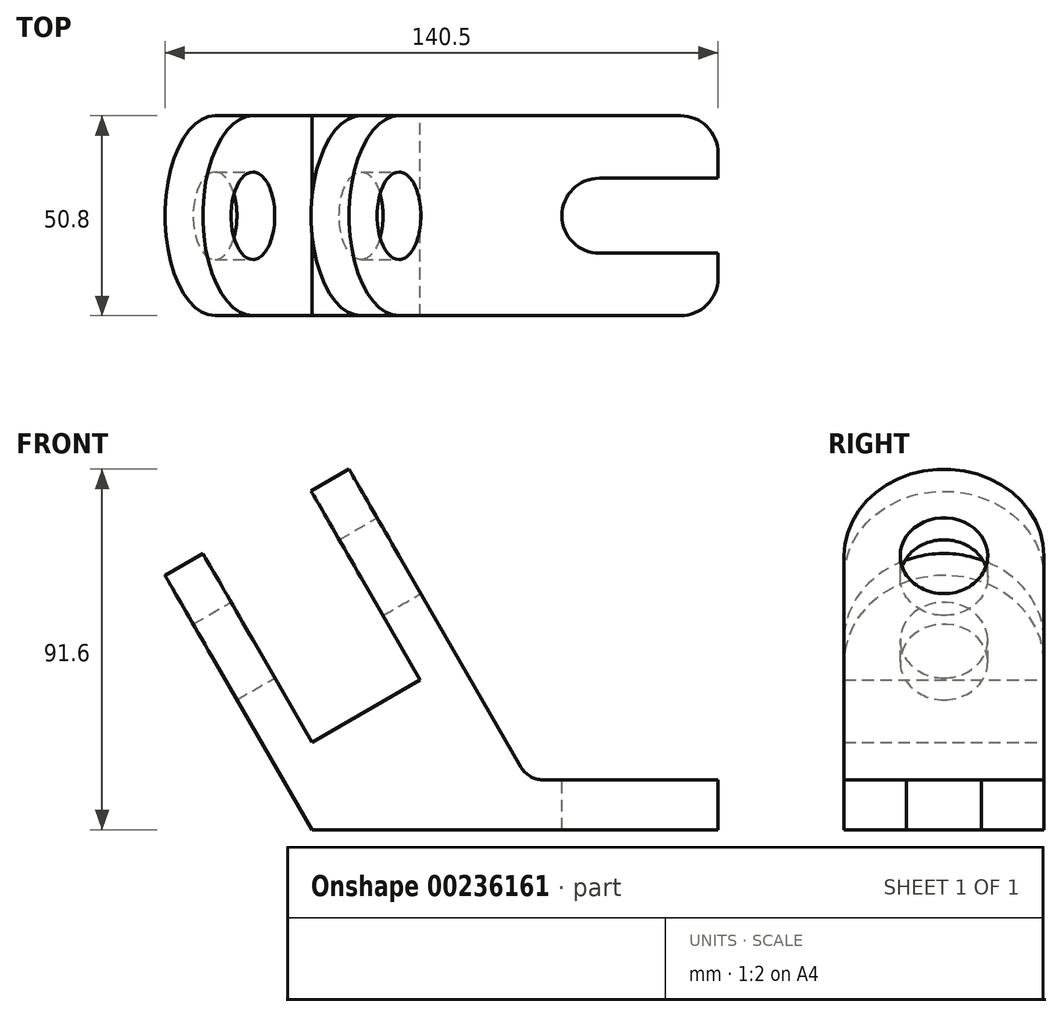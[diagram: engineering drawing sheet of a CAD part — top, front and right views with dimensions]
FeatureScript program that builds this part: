
annotation { "Feature Type Name" : "Feature", "Feature Type Description" : "" }
export const myFeature = defineFeature(function(context is Context, id is Id, definition is map)
    precondition{}
    {
        {
            var Q0;
            Q0=qCreatedBy(makeId("Front.planeOp"),FACE);
            var sketch = newSketch(context, id + "F0", { "sketchPlane" : qUnion([Q0])});
            skLineSegment(sketch, "E0", {"start": v(0, 0) * mm, "end": v(103.19, 0) * mm});
            skLineSegment(sketch, "E1", {"start": v(103.19, 0) * mm, "end": v(103.19, 12.7) * mm});
            skLineSegment(sketch, "E2", {"start": v(103.19, 12.7) * mm, "end": v(58.66, 12.7) * mm});
            skLineSegment(sketch, "E3", {"start": v(53.16, 15.88) * mm, "end": v(9.44, 91.6) * mm});
            skLineSegment(sketch, "E4", {"start": v(9.44, 91.6) * mm, "end": v(-0.19, 86.05) * mm});
            skLineSegment(sketch, "E5", {"start": v(-37.3, 64.62) * mm, "end": v(0, 0) * mm});
            skLineSegment(sketch, "E6", {"start": v(-27.68, 70.17) * mm, "end": v(0, 22.22) * mm});
            skLineSegment(sketch, "E7", {"start": v(0, 22.23) * mm, "end": v(27.5, 38.1) * mm});
            skLineSegment(sketch, "E8", {"start": v(27.5, 38.1) * mm, "end": v(-0.19, 86.05) * mm});
            skLineSegment(sketch, "E9.trimOffspring", {"start": v(-27.68, 70.17) * mm, "end": v(-37.3, 64.62) * mm});
            skPoint(sketch, "E10.visualSharp", {"position": v(55, 12.7) * mm});
            skArc(sketch, "E10.filletArc", {"start": v(53.16, 15.88) * mm, "mid": v(55.48, 13.55) * mm, "end": v(58.66, 12.7) * mm});
            skSolve(sketch);
        }
        {
            var Q0;
            Q0=makeQuery(id+"F0.imprint","IMPRINT",FACE,{"disambiguationData":[TD([[makeQuery(id+"F0.imprint","IMPRINT",EDGE,{"derivedFrom":sQuery(id+"F0.wireOp",EDGE,"E0")}),1.0]])]});
            extrude(context, id + "F1", {"entities" : qUnion([Q0]), "endBound" : BoundingType.SYMMETRIC, "depth" : 50.8 * mm});
        }
        {
            var Q0;
            Q0=makeQuery(id+"F1.opExtrude","SWEPT_FACE",FACE,{"disambiguationData":[OSD([sQuery(id+"F0.wireOp",EDGE,"E2")])]});
            var sketch = newSketch(context, id + "F2", { "sketchPlane" : qUnion([Q0])});
            skArc(sketch, "E11", {"start": v(73.03, 9.53) * mm, "mid": v(63.5, 0) * mm, "end": v(73.03, -9.53) * mm});
            skPoint(sketch, "E11.centerSnap0", {"position": v(103.19, 0) * mm});
            skLineSegment(sketch, "E12", {"start": v(73.03, 9.53) * mm, "end": v(103.19, 9.53) * mm});
            skLineSegment(sketch, "E13", {"start": v(73.03, -9.53) * mm, "end": v(103.19, -9.52) * mm});
            skLineSegment(sketch, "E14.0", {"start": v(103.19, -9.53) * mm, "end": v(103.19, 9.52) * mm});
            skPoint(sketch, "E15.orphan", {"position": v(103.19, 25.4) * mm});
            skPoint(sketch, "E16.orphan", {"position": v(103.19, -25.4) * mm});
            skSolve(sketch);
        }
        {
            var Q0;
            Q0=makeQuery(id+"F2.imprint","IMPRINT",FACE,{"disambiguationData":[TD([[makeQuery(id+"F2.imprint","IMPRINT",EDGE,{"derivedFrom":sQuery(id+"F2.wireOp",EDGE,"E11")}),1.0]])]});
            extrude(context, id + "F3", {"entities" : qUnion([Q0]), "operationType" : NewBodyOperationType.REMOVE, "endBound" : BoundingType.THROUGH_ALL, "oppositeDirection" : true, "depth" : 25.4 * mm});
        }
        {
            var Q0;
            Q0=makeQuery(id+"F1.opExtrude","SWEPT_FACE",FACE,{"disambiguationData":[OSD([sQuery(id+"F0.wireOp",EDGE,"E3")])]});
            var sketch = newSketch(context, id + "F4", { "sketchPlane" : qUnion([Q0])});
            skPoint(sketch, "E17", {"position": v(0, 49.21) * mm});
            skPoint(sketch, "E17.positionSnap0", {"position": v(0, 74.61) * mm});
            skSolve(sketch);
        }
        {
            var Q0;
            Q0=sQuery(id+"F4.wireOp",VERTEX,"E17");
            var Q1;
            Q1=makeQuery(id+"F1.opExtrude","SWEPT_BODY",BODY,{"disambiguationData":[OSD([sQuery(id+"F0.wireOp",EDGE,"E0"),sQuery(id+"F0.wireOp",EDGE,"E1"),sQuery(id+"F0.wireOp",EDGE,"E2"),sQuery(id+"F0.wireOp",EDGE,"E3"),sQuery(id+"F0.wireOp",EDGE,"E4"),sQuery(id+"F0.wireOp",EDGE,"E5"),sQuery(id+"F0.wireOp",EDGE,"E6"),sQuery(id+"F0.wireOp",EDGE,"E7"),sQuery(id+"F0.wireOp",EDGE,"E8"),sQuery(id+"F0.wireOp",EDGE,"E9.trimOffspring"),sQuery(id+"F0.wireOp",EDGE,"E10.filletArc")])]});
            hole(context, id + "F5", {"style" : HoleStyle.SIMPLE, "endStyle" : HoleEndStyle.THROUGH, "holeDiameter" : 22.22 * mm, "locations" : qUnion([Q0]), "scope" : qUnion([Q1]), "isTappedThrough" : true});
        }
        {
            var Q0;
            Q0=makeQuery(id+"F1.opExtrude","CAP_EDGE",EDGE,{"disambiguationData":[OSD([sQuery(id+"F0.wireOp",EDGE,"E9.trimOffspring")])],"isStart":true});
            var Q1;
            Q1=makeQuery(id+"F1.opExtrude","CAP_EDGE",EDGE,{"disambiguationData":[OSD([sQuery(id+"F0.wireOp",EDGE,"E4")])],"isStart":true});
            var Q2;
            Q2=makeQuery(id+"F1.opExtrude","CAP_EDGE",EDGE,{"disambiguationData":[OSD([sQuery(id+"F0.wireOp",EDGE,"E9.trimOffspring")])],"isStart":false});
            var Q3;
            Q3=makeQuery(id+"F1.opExtrude","CAP_EDGE",EDGE,{"disambiguationData":[OSD([sQuery(id+"F0.wireOp",EDGE,"E4")])],"isStart":false});
            fillet(context, id + "F6", {"entities" : qUnion([Q0, Q1, Q2, Q3]), "radius" : 25.4 * mm, "tangentPropagation" : true, "allowEdgeOverflow" : false});
        }
        {
            var Q0;
            Q0=makeQuery(id+"F1.opExtrude","CAP_EDGE",EDGE,{"disambiguationData":[OSD([sQuery(id+"F0.wireOp",EDGE,"E1")])],"isStart":true});
            var Q1;
            Q1=makeQuery(id+"F1.opExtrude","CAP_EDGE",EDGE,{"disambiguationData":[OSD([sQuery(id+"F0.wireOp",EDGE,"E1")])],"isStart":false});
            fillet(context, id + "F7", {"entities" : qUnion([Q0, Q1]), "radius" : 9.52 * mm, "tangentPropagation" : true, "allowEdgeOverflow" : false});
        }
    });
